# Revit family: ir_180_universal_033149
name_source: partatom
category: Elektroinstallationen
revit_build: Autodesk Revit 2016 (Build: 20190508_0715(x64)
units: mm (PartAtom-declared; Revit-internal decimal feet)

## family parameters
Basisbauteil = Fläche
Beim Laden mit Abzugskörper schneiden = Nein
Bemaßung runder Anschluss = Durchmesser verwenden
Beschriftungsausrichtung beibehalten = Nein
Gemeinsam genutzt = Nein
Raumberechnungspunkt = Nein
Teiletyp = Normal

## types (1)
- IR 180 UNIVERSAL
    Apparent Load = 0 VA
    Beschreibung = Type: Presence detector; Dimensions (L x W x H): 21 x 80 x 80 mm; Mains power supply: 220 – 240 V / 50 – 60 Hz; Sensor Technology: passive infrared; Application, place: Indoors; Application, room: one-person office, corridor / aisle, function room / ancillary room, kitchenette, stairwell, WC / washroom, Indoors; Installation site: wall; Installation: Concealed wiring; Switching zones: 96 switching zones; Electronic scalability: Yes; Mechanical scalability: No; Mounting height: 1,10 – 1,20 m; Optimum mounting height: 1,2 m; Detection angle: 180 °; Angle of aperture: 90 °; Sneak-by guard: Yes; Reach, radial: r = 4 m (25 m²); Reach, tangential: r = 20 m (628 m²); Reach, presence: r = 4 m (25 m²); Twilight setting TEACH: Yes; Twilight setting: 2 – 1000 lx; Time setting: 30 sec – 15 min; Switching output 1, resistive: 200 W; Switching output 1, number of LEDs / fluorescent lamps: 6 pcs.; Constant-lighting control: No; Basic light level function: No; Functions: Switch active / switch inactive, Normal / test mode, Manual ON / ON-OFF; Settings via: Remote control, Potentiometers, Smart Remote; With remote control: No; Interconnection: Yes; IP-rating: IP20; Material: Plastic; Ambient temperature: 0 – 40 °C; Colour: white; Colour, RAL: 9010; IDs, certificates: KEMA; Manufacturer's Warranty: 5 years; Version: white; PU1, EAN: 4007841033149
    Height = 80 mm  [stored 0.262467 ft]
    Hersteller = Steinel
    Length = 21 mm
    Maximum range = 8.434 m
    ModVariant = Nein
    Modell = 033149
    Mounting Type = Recessed
    Number of Poles = 1
    OnlyDefault = Ja
    Power Factor = 1
    Product Name = IR 180 UNIVERSAL
    Product group = Sensor-switched indoor light
    ProductGroupID = 30
    Protection Class = Protection class
    Protection Degree = IP 20
    RlxData = <blob elided: 149581 chars, md5=a481b969>
    Sensor characteristics = Semi circular 145°-300°
    Sensor type = Passive (infrared)
    SensorDataFile = <blob elided: 4559 chars, md5=eaf032c5>
    Type of entry = Motion
    Typenbild = produkt1_033149.jpg
    Typenkommentare = Product without accessories
    URL = http://relux.com
    VarID = ---
    Voltage = 0 V
    Vorgabe-Ansicht = 1800 mm
    Weight = 0.00 kg
    Width = 80 mm  [stored 0.262467 ft]

note: [stored X ft] marks values corroborated as IEEE doubles in the binary element streams (Revit-internal decimal feet)

## geometry (parser evidence)
native form markers: Blend x4, Sweep x20
no freeform markers — native parametric forms only
